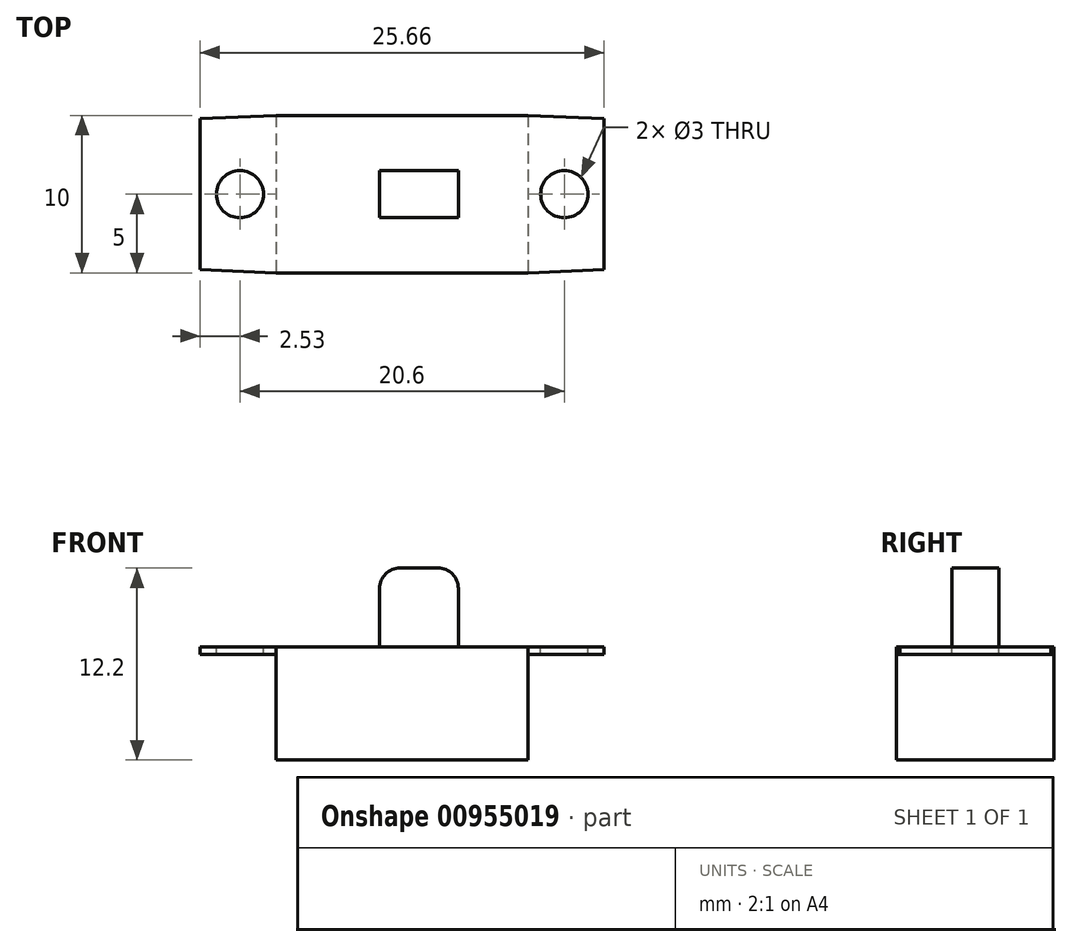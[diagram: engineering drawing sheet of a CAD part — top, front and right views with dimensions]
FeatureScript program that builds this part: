
annotation { "Feature Type Name" : "Feature", "Feature Type Description" : "" }
export const myFeature = defineFeature(function(context is Context, id is Id, definition is map)
    precondition{}
    {
        {
            var Q0;
            Q0=qCreatedBy(makeId("Top.planeOp"),FACE);
            var sketch = newSketch(context, id + "F0", { "sketchPlane" : qUnion([Q0])});
            skLineSegment(sketch, "E0.bottom", {"start": v(8, 5) * mm, "end": v(-8, 5) * mm});
            skLineSegment(sketch, "E0.top", {"start": v(8, -5) * mm, "end": v(-8, -5) * mm});
            skLineSegment(sketch, "E0.left", {"start": v(8, 5) * mm, "end": v(8, -5) * mm});
            skLineSegment(sketch, "E0.right", {"start": v(-8, 5) * mm, "end": v(-8, -5) * mm});
            skPoint(sketch, "E0.middle", {"position": v(0, 0) * mm});
            skSolve(sketch);
        }
        {
            var Q0;
            Q0 = qSketchRegion(id + "F0", true);
            extrude(context, id + "F1", {"entities" : qUnion([Q0]), "depth" : 7.2 * mm, "offsetDistance" : 25 * mm});
        }
        {
            var Q0;
            Q0=makeQuery(id+"F1.opExtrude","CAP_FACE",FACE,{"disambiguationData":[OSD([sQuery(id+"F0.wireOp",EDGE,"E0.bottom"),sQuery(id+"F0.wireOp",EDGE,"E0.top"),sQuery(id+"F0.wireOp",EDGE,"E0.left"),sQuery(id+"F0.wireOp",EDGE,"E0.right")])],"isStart":false});
            var sketch = newSketch(context, id + "F2", { "sketchPlane" : qUnion([Q0])});
            skLineSegment(sketch, "E1.bottom", {"start": v(3.57, 1.5) * mm, "end": v(-1.43, 1.5) * mm});
            skLineSegment(sketch, "E1.top", {"start": v(3.57, -1.5) * mm, "end": v(-1.43, -1.5) * mm});
            skLineSegment(sketch, "E1.left", {"start": v(3.57, 1.5) * mm, "end": v(3.57, -1.5) * mm});
            skLineSegment(sketch, "E1.right", {"start": v(-1.43, 1.5) * mm, "end": v(-1.43, -1.5) * mm});
            skPoint(sketch, "E1.middle", {"position": v(1.07, 0) * mm});
            skSolve(sketch);
        }
        {
            var Q0;
            Q0 = qSketchRegion(id + "F2", true);
            extrude(context, id + "F3", {"entities" : qUnion([Q0]), "operationType" : NewBodyOperationType.ADD, "depth" : 5 * mm, "offsetDistance" : 25 * mm});
        }
        {
            var Q0;
            Q0=makeQuery(id+"F3.opExtrude","CAP_EDGE",EDGE,{"disambiguationData":[OSD([sQuery(id+"F2.wireOp",EDGE,"E1.right")])],"isStart":false});
            var Q1;
            Q1=makeQuery(id+"F3.opExtrude","CAP_EDGE",EDGE,{"disambiguationData":[OSD([sQuery(id+"F2.wireOp",EDGE,"E1.left")])],"isStart":false});
            fillet(context, id + "F4", {"entities" : qUnion([Q0, Q1]), "radius" : 1.3 * mm, "tangentPropagation" : true, "allowEdgeOverflow" : false});
        }
        {
            var Q0;
            Q0=makeQuery(id+"F1.opExtrude","CAP_FACE",FACE,{"disambiguationData":[OSD([sQuery(id+"F0.wireOp",EDGE,"E0.bottom"),sQuery(id+"F0.wireOp",EDGE,"E0.top"),sQuery(id+"F0.wireOp",EDGE,"E0.left"),sQuery(id+"F0.wireOp",EDGE,"E0.right")])],"isStart":false});
            var sketch = newSketch(context, id + "F5", { "sketchPlane" : qUnion([Q0])});
            skLineSegment(sketch, "E2", {"start": v(-8, 5) * mm, "end": v(0, 5) * mm});
            skLineSegment(sketch, "E3", {"start": v(-8, 5) * mm, "end": v(-12.83, 4.8) * mm});
            skLineSegment(sketch, "E4", {"start": v(-12.83, 4.8) * mm, "end": v(-12.83, 0) * mm});
            skLineSegment(sketch, "E5", {"start": v(0, 0) * mm, "end": v(-31.16, 0) * mm, "construction": true});
            skLineSegment(sketch, "E6", {"start": v(0, 0) * mm, "end": v(0, -18.65) * mm, "construction": true});
            skPoint(sketch, "E6.endSnap0", {"position": v(0, -5) * mm});
            skLineSegment(sketch, "E7.MirrorCS", {"start": v(8, 5) * mm, "end": v(0, 5) * mm});
            skLineSegment(sketch, "E8.MirrorCS", {"start": v(12.83, 4.8) * mm, "end": v(12.83, 0) * mm});
            skLineSegment(sketch, "E9.MirrorCS", {"start": v(8, 5) * mm, "end": v(12.83, 4.8) * mm});
            skLineSegment(sketch, "E10.MirrorCS", {"start": v(12.83, -4.8) * mm, "end": v(12.83, 0) * mm});
            skLineSegment(sketch, "E11.MirrorCS", {"start": v(-12.83, -4.8) * mm, "end": v(-12.83, 0) * mm});
            skLineSegment(sketch, "E12.MirrorCS", {"start": v(-8, -5) * mm, "end": v(-12.83, -4.8) * mm});
            skLineSegment(sketch, "E13.MirrorCS", {"start": v(8, -5) * mm, "end": v(12.83, -4.8) * mm});
            skLineSegment(sketch, "E14.MirrorCS", {"start": v(8, -5) * mm, "end": v(0, -5) * mm});
            skLineSegment(sketch, "E15.MirrorCS", {"start": v(-8, -5) * mm, "end": v(0, -5) * mm});
            skCircle(sketch, "E16", {"center": v(-10.3, 0) * mm, "radius": 1.5 * mm});
            skCircle(sketch, "E17.MirrorC", {"center": v(10.3, 0) * mm, "radius": 1.5 * mm});
            skSolve(sketch);
        }
        {
            var Q0;
            Q0 = qSketchRegion(id + "F5", true);
            extrude(context, id + "F6", {"entities" : qUnion([Q0]), "operationType" : NewBodyOperationType.ADD, "oppositeDirection" : true, "depth" : .5 * mm, "offsetDistance" : 25 * mm});
        }
    });
